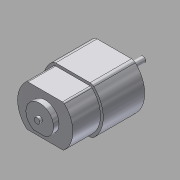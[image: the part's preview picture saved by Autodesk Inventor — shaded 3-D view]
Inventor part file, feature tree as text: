
AUTODESK INVENTOR PART (.ipt)
format: ipt  version: 2015 (Build 190159000, 159)  size: 137,728 bytes
history: native  units: in
note: dims shown in document units (in); Inventor stores cm internally (conversion verified against a paired STEP export)
features: sketch x5, other x3
ambient origin geometry x8: Origin, YZ Plane, XZ Plane, XY Plane, X Axis, Y Axis, Z Axis, Center Point
bodies: Solid1 (feature_tree)
feature tree (8):
  other  "motor.ipt"
  other  "Solid1::motor.ipt"
  other  "TaggingFeature1"
  sketch  "Sketch1"  dims[d0=0.3937in]
  sketch  "Sketch2"
  sketch  "Sketch3"
  sketch  "Sketch4"
  sketch  "Sketch5"
